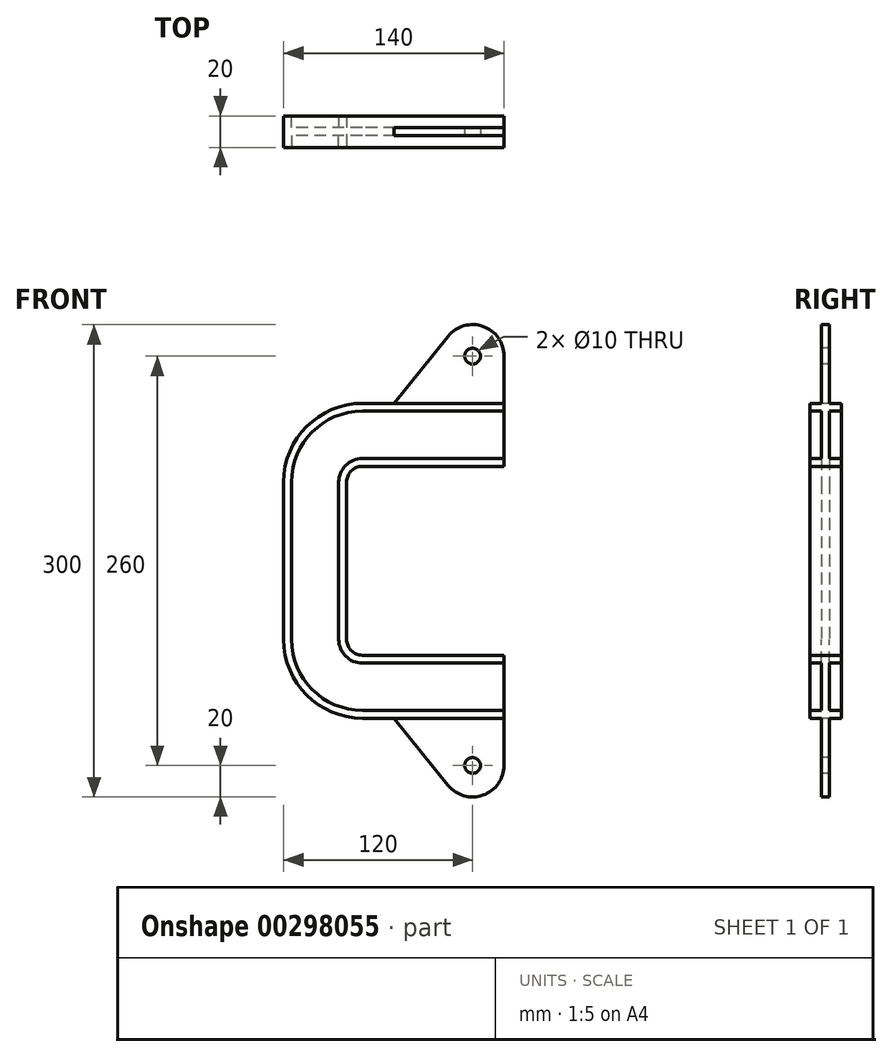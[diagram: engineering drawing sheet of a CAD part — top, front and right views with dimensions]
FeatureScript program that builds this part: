
annotation { "Feature Type Name" : "Feature", "Feature Type Description" : "" }
export const myFeature = defineFeature(function(context is Context, id is Id, definition is map)
    precondition{}
    {
        {
            var Q0;
            Q0=qCreatedBy(makeId("Front.planeOp"),FACE);
            var sketch = newSketch(context, id + "F0", { "sketchPlane" : qUnion([Q0])});
            skLineSegment(sketch, "E0", {"start": v(0, 60) * mm, "end": v(-90, 60) * mm});
            skLineSegment(sketch, "E1", {"start": v(-100, 50) * mm, "end": v(-100, 0) * mm});
            skPoint(sketch, "E2.visualSharp", {"position": v(-100, 60) * mm});
            skArc(sketch, "E2.filletArc", {"start": v(-90, 60) * mm, "mid": v(-97.07, 57.07) * mm, "end": v(-100, 50) * mm});
            skSolve(sketch);
        }
        {
            var Q0;
            Q0=qCreatedBy(makeId("Right.planeOp"),FACE);
            var sketch = newSketch(context, id + "F1", { "sketchPlane" : qUnion([Q0])});
            skLineSegment(sketch, "E3", {"start": v(0, 0) * mm, "end": v(0, 60) * mm, "construction": true});
            skLineSegment(sketch, "E4", {"start": v(0, 60) * mm, "end": v(10, 60) * mm});
            skLineSegment(sketch, "E5", {"start": v(10, 60) * mm, "end": v(10, 65) * mm});
            skLineSegment(sketch, "E6", {"start": v(10, 65) * mm, "end": v(2.5, 65) * mm});
            skLineSegment(sketch, "E7", {"start": v(2.5, 65) * mm, "end": v(2.5, 95) * mm});
            skLineSegment(sketch, "E8", {"start": v(2.5, 95) * mm, "end": v(10, 95) * mm});
            skLineSegment(sketch, "E9", {"start": v(10, 95) * mm, "end": v(10, 100) * mm});
            skLineSegment(sketch, "E10", {"start": v(10, 100) * mm, "end": v(0, 100) * mm});
            skLineSegment(sketch, "E11", {"start": v(0, 100) * mm, "end": v(0, 60) * mm, "construction": true});
            skLineSegment(sketch, "E12.MirrorCS", {"start": v(-10, 65) * mm, "end": v(-2.5, 65) * mm});
            skLineSegment(sketch, "E13.MirrorCS", {"start": v(-10, 60) * mm, "end": v(-10, 65) * mm});
            skLineSegment(sketch, "E14.MirrorCS", {"start": v(-2.5, 65) * mm, "end": v(-2.5, 95) * mm});
            skLineSegment(sketch, "E15.MirrorCS", {"start": v(-2.5, 95) * mm, "end": v(-10, 95) * mm});
            skLineSegment(sketch, "E16.MirrorCS", {"start": v(0, 60) * mm, "end": v(-10, 60) * mm});
            skLineSegment(sketch, "E17.MirrorCS", {"start": v(-10, 95) * mm, "end": v(-10, 100) * mm});
            skLineSegment(sketch, "E18.MirrorCS", {"start": v(-10, 100) * mm, "end": v(0, 100) * mm});
            skSolve(sketch);
        }
        {
            var Q0;
            Q0=makeQuery(id+"F1.imprint","IMPRINT",FACE,{"disambiguationData":[TD([[makeQuery(id+"F1.imprint","IMPRINT",EDGE,{"derivedFrom":sQuery(id+"F1.wireOp",EDGE,"E4")}),1.0]])]});
            var Q1;
            Q1=sQuery(id+"F0.wireOp",EDGE,"E0");
            var Q2;
            Q2=sQuery(id+"F0.wireOp",EDGE,"E2.filletArc");
            var Q3;
            Q3=sQuery(id+"F0.wireOp",EDGE,"E1");
            sweep(context, id + "F2", {"profiles" : qUnion([Q0]), "path" : qUnion([Q1, Q2, Q3])});
        }
        {
            var Q0;
            Q0=qCreatedBy(makeId("Front.planeOp"),FACE);
            var sketch = newSketch(context, id + "F3", { "sketchPlane" : qUnion([Q0])});
            skLineSegment(sketch, "E19", {"start": v(0, 100) * mm, "end": v(0, 130) * mm});
            skArc(sketch, "E20", {"start": v(0, 130) * mm, "mid": v(-13.33, 148.85) * mm, "end": v(-35.55, 142.58) * mm});
            skLineSegment(sketch, "E21", {"start": v(-35.55, 142.58) * mm, "end": v(-70, 100) * mm});
            skLineSegment(sketch, "E22", {"start": v(-70, 100) * mm, "end": v(0, 100) * mm});
            skCircle(sketch, "E23", {"center": v(-20, 130) * mm, "radius": 5 * mm});
            skSolve(sketch);
        }
        {
            var Q0;
            Q0=makeQuery(id+"F3.imprint","IMPRINT",FACE,{"disambiguationData":[TD([[makeQuery(id+"F3.imprint","IMPRINT",EDGE,{"derivedFrom":sQuery(id+"F3.wireOp",EDGE,"E19")}),1.0]])]});
            extrude(context, id + "F4", {"entities" : qUnion([Q0]), "operationType" : NewBodyOperationType.ADD, "endBound" : BoundingType.SYMMETRIC, "oppositeDirection" : true, "depth" : 5 * mm});
        }
        {
            var Q0;
            Q0=makeQuery(id+"F2.opSweep","SWEPT_BODY",BODY,{"disambiguationData":[OSD([sQuery(id+"F0.wireOp",EDGE,"E1"),sQuery(id+"F1.wireOp",EDGE,"E4"),sQuery(id+"F1.wireOp",EDGE,"E5"),sQuery(id+"F1.wireOp",EDGE,"E6"),sQuery(id+"F1.wireOp",EDGE,"E7"),sQuery(id+"F1.wireOp",EDGE,"E8"),sQuery(id+"F1.wireOp",EDGE,"E9"),sQuery(id+"F1.wireOp",EDGE,"E10"),sQuery(id+"F1.wireOp",EDGE,"E12.MirrorCS"),sQuery(id+"F1.wireOp",EDGE,"E13.MirrorCS"),sQuery(id+"F1.wireOp",EDGE,"E14.MirrorCS"),sQuery(id+"F1.wireOp",EDGE,"E15.MirrorCS"),sQuery(id+"F1.wireOp",EDGE,"E16.MirrorCS"),sQuery(id+"F1.wireOp",EDGE,"E17.MirrorCS"),sQuery(id+"F1.wireOp",EDGE,"E18.MirrorCS")])]});
            var Q1;
            Q1=qCreatedBy(makeId("Top.planeOp"),FACE);
            mirror(context, id + "F5", {"operationType" : NewBodyOperationType.ADD, "entities" : qUnion([Q0]), "mirrorPlane" : qUnion([Q1])});
        }
    });
